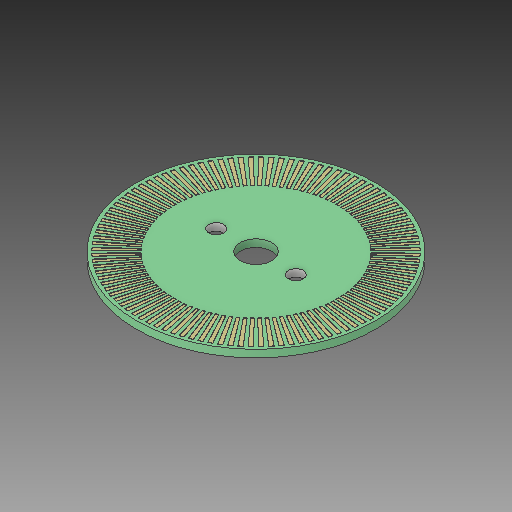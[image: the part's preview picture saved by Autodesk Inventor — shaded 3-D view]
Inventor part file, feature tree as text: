
AUTODESK INVENTOR PART (.ipt)
format: ipt  version: 2018 (Build 220112000, 112)  size: 908,288 bytes
history: native  units: mm
features: extrude x3, sketch x3, pattern_circular x1, plane x1, mirror x1
ambient origin geometry x8: Origin, YZ Plane, XZ Plane, XY Plane, X Axis, Y Axis, Z Axis, Center Point
bodies: Solid1 (feature_tree)
feature tree (9):
  extrude  "Extrusion1"  Depth=6.35mm
  extrude  "Extrusion2"  Depth=1.5mm
  pattern_circular  "Circular Pattern1"  [2 undecoded]
  plane  "Work Plane1"
  mirror  "Mirror1"
  extrude  "Extrusion3"  Depth=0.1mm TaperAngle=0.0deg
  sketch  "Sketch1"  dims[d0=48.0mm d1=6.35mm]
  sketch  "Sketch2"  dims[d2=1.5mm d3=0.0mm d4=0.7mm]
  sketch  "Sketch4"  dims[d5=7.0mm d6=0.75mm d7=0.1mm d8=0.0mm d9=1000.0mm d10=360.0deg d12=0.524678mm d23=8.0mm d24=8.0mm d25=3.0mm d26=3.0mm d27=10.0mm d28=0.0mm]
note: 2 required parameter values undecoded (feature->parameter linkage not recoverable at this tier; creation-order binding heuristic only, values carry confidence <= 0.55)
